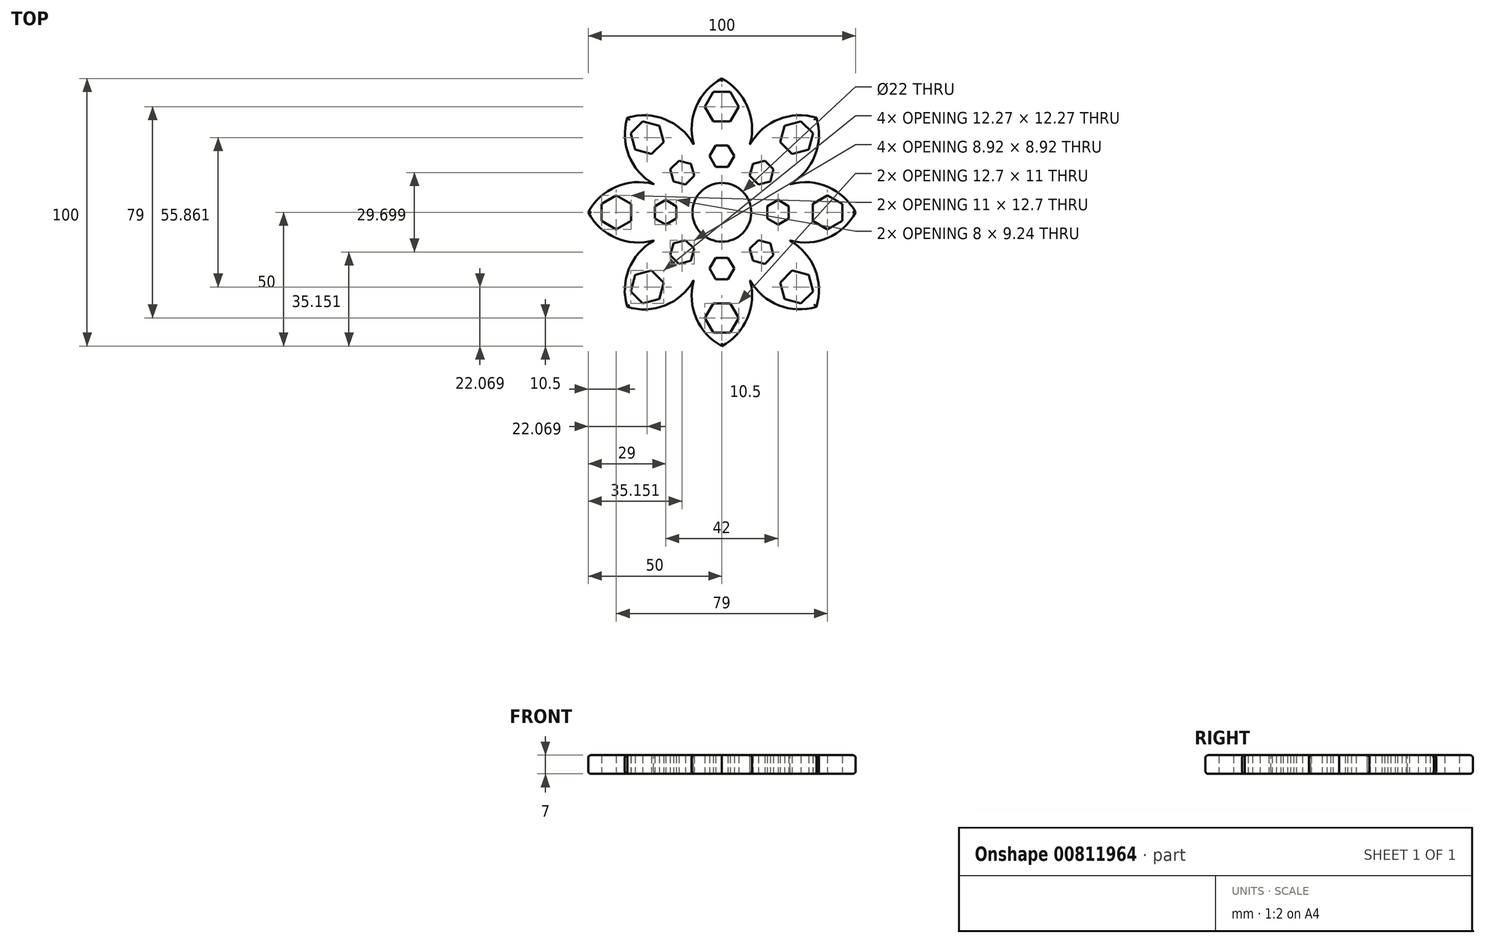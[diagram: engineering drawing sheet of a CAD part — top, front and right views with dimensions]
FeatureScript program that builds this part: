
annotation { "Feature Type Name" : "Feature", "Feature Type Description" : "" }
export const myFeature = defineFeature(function(context is Context, id is Id, definition is map)
    precondition{}
    {
        {
            var Q0;
            Q0=qCreatedBy(makeId("Top.planeOp"),FACE);
            var sketch = newSketch(context, id + "F0", { "sketchPlane" : qUnion([Q0])});
            skCircle(sketch, "E0", {"center": v(0, 0) * mm, "radius": 11 * mm});
            skLineSegment(sketch, "E1", {"start": v(0, 74.6) * mm, "end": v(0, -73.86) * mm, "construction": true});
            skLineSegment(sketch, "E2", {"start": v(-71.42, 0) * mm, "end": v(71.7, 0) * mm, "construction": true});
            skLineSegment(sketch, "E3", {"start": v(75.06, 75.06) * mm, "end": v(0, 0) * mm, "construction": true});
            skLineSegment(sketch, "E4", {"start": v(0, 0) * mm, "end": v(-70.75, -70.75) * mm, "construction": true});
            skLineSegment(sketch, "E5", {"start": v(-75.13, 75.13) * mm, "end": v(0, 0) * mm, "construction": true});
            skCircle(sketch, "E6.cCircle", {"center": v(0, 0) * mm, "radius": 21 * mm, "construction": true});
            skLineSegment(sketch, "E6.0", {"start": v(-8.7, 21) * mm, "end": v(8.7, 21) * mm});
            skLineSegment(sketch, "E6.1", {"start": v(8.7, 21) * mm, "end": v(21, 8.7) * mm});
            skLineSegment(sketch, "E6.2", {"start": v(21, 8.7) * mm, "end": v(21, -8.7) * mm});
            skLineSegment(sketch, "E6.3", {"start": v(21, -8.7) * mm, "end": v(8.7, -21) * mm});
            skLineSegment(sketch, "E6.4", {"start": v(8.7, -21) * mm, "end": v(-8.7, -21) * mm});
            skLineSegment(sketch, "E6.5", {"start": v(-8.7, -21) * mm, "end": v(-21, -8.7) * mm});
            skLineSegment(sketch, "E6.6", {"start": v(-21, -8.7) * mm, "end": v(-21, 8.7) * mm});
            skLineSegment(sketch, "E6.7", {"start": v(-21, 8.7) * mm, "end": v(-8.7, 21) * mm});
            skPoint(sketch, "E6.0.midPoint", {"position": v(0, 21) * mm});
            skLineSegment(sketch, "E7", {"start": v(0, 21) * mm, "end": v(0, 50) * mm});
            skLineSegment(sketch, "E8", {"start": v(14.85, 14.85) * mm, "end": v(35.38, 35.38) * mm});
            skLineSegment(sketch, "E9", {"start": v(21, 0) * mm, "end": v(50, 0) * mm});
            skLineSegment(sketch, "E10", {"start": v(14.85, -14.85) * mm, "end": v(35.36, -35.36) * mm});
            skLineSegment(sketch, "E11", {"start": v(0, -21) * mm, "end": v(0, -50) * mm});
            skLineSegment(sketch, "E12", {"start": v(-14.85, -14.85) * mm, "end": v(-35.38, -35.38) * mm});
            skLineSegment(sketch, "E13", {"start": v(-21, 0) * mm, "end": v(-50, 0) * mm});
            skLineSegment(sketch, "E14", {"start": v(-14.85, 14.85) * mm, "end": v(-35.36, 35.36) * mm});
            skArc(sketch, "E15", {"start": v(0, 50) * mm, "mid": v(-10.4, 37.31) * mm, "end": v(-8.7, 21) * mm});
            skArc(sketch, "E16.MirrorCS", {"start": v(0, 50) * mm, "mid": v(10.4, 37.31) * mm, "end": v(8.7, 21) * mm});
            skArc(sketch, "E17", {"start": v(35.38, 35.38) * mm, "mid": v(19.04, 33.76) * mm, "end": v(8.7, 21) * mm});
            skArc(sketch, "E18.MirrorCS", {"start": v(35.38, 35.38) * mm, "mid": v(33.76, 19.04) * mm, "end": v(21, 8.7) * mm});
            skArc(sketch, "E19", {"start": v(50, 0) * mm, "mid": v(37.31, 10.4) * mm, "end": v(21, 8.7) * mm});
            skArc(sketch, "E20.MirrorCS", {"start": v(50, 0) * mm, "mid": v(37.31, -10.4) * mm, "end": v(21, -8.7) * mm});
            skArc(sketch, "E21", {"start": v(35.36, -35.36) * mm, "mid": v(33.74, -19.03) * mm, "end": v(21, -8.7) * mm});
            skArc(sketch, "E22.MirrorCS", {"start": v(35.36, -35.36) * mm, "mid": v(19.03, -33.74) * mm, "end": v(8.7, -21) * mm});
            skArc(sketch, "E23", {"start": v(0, -50) * mm, "mid": v(10.4, -37.31) * mm, "end": v(8.7, -21) * mm});
            skArc(sketch, "E24.MirrorCS", {"start": v(0, -50) * mm, "mid": v(-10.4, -37.31) * mm, "end": v(-8.7, -21) * mm});
            skArc(sketch, "E25", {"start": v(-35.38, -35.38) * mm, "mid": v(-19.04, -33.76) * mm, "end": v(-8.7, -21) * mm});
            skArc(sketch, "E26.MirrorCS", {"start": v(-35.38, -35.38) * mm, "mid": v(-33.76, -19.04) * mm, "end": v(-21, -8.7) * mm});
            skArc(sketch, "E27", {"start": v(-50, 0) * mm, "mid": v(-37.31, -10.4) * mm, "end": v(-21, -8.7) * mm});
            skArc(sketch, "E28.MirrorCS", {"start": v(-50, 0) * mm, "mid": v(-37.31, 10.4) * mm, "end": v(-21, 8.7) * mm});
            skArc(sketch, "E29", {"start": v(-35.36, 35.36) * mm, "mid": v(-33.74, 19.03) * mm, "end": v(-21, 8.7) * mm});
            skArc(sketch, "E30.MirrorCS", {"start": v(-35.36, 35.36) * mm, "mid": v(-19.03, 33.74) * mm, "end": v(-8.7, 21) * mm});
            skCircle(sketch, "E31.cCircle", {"center": v(27.93, 27.93) * mm, "radius": 5.5 * mm, "construction": true});
            skLineSegment(sketch, "E31.0", {"start": v(23.44, 32.42) * mm, "end": v(29.57, 34.07) * mm});
            skLineSegment(sketch, "E31.1", {"start": v(29.57, 34.07) * mm, "end": v(34.07, 29.57) * mm});
            skLineSegment(sketch, "E31.2", {"start": v(34.07, 29.57) * mm, "end": v(32.42, 23.44) * mm});
            skLineSegment(sketch, "E31.3", {"start": v(32.42, 23.44) * mm, "end": v(26.29, 21.8) * mm});
            skLineSegment(sketch, "E31.4", {"start": v(26.29, 21.8) * mm, "end": v(21.8, 26.29) * mm});
            skLineSegment(sketch, "E31.5", {"start": v(21.8, 26.29) * mm, "end": v(23.44, 32.42) * mm});
            skPoint(sketch, "E31.0.midPoint", {"position": v(26.5, 33.24) * mm});
            skCircle(sketch, "E32.cCircle", {"center": v(39.5, 0) * mm, "radius": 5.5 * mm, "construction": true});
            skLineSegment(sketch, "E32.0", {"start": v(39.5, 6.35) * mm, "end": v(45, 3.18) * mm});
            skLineSegment(sketch, "E32.1", {"start": v(45, 3.18) * mm, "end": v(45, -3.18) * mm});
            skLineSegment(sketch, "E32.2", {"start": v(45, -3.18) * mm, "end": v(39.5, -6.35) * mm});
            skLineSegment(sketch, "E32.3", {"start": v(39.5, -6.35) * mm, "end": v(34, -3.18) * mm});
            skLineSegment(sketch, "E32.4", {"start": v(34, -3.18) * mm, "end": v(34, 3.18) * mm});
            skLineSegment(sketch, "E32.5", {"start": v(34, 3.18) * mm, "end": v(39.5, 6.35) * mm});
            skPoint(sketch, "E32.0.midPoint", {"position": v(42.25, 4.76) * mm});
            skCircle(sketch, "E33.cCircle", {"center": v(-27.93, -27.93) * mm, "radius": 5.5 * mm, "construction": true});
            skLineSegment(sketch, "E33.0", {"start": v(-23.44, -32.42) * mm, "end": v(-29.57, -34.07) * mm});
            skLineSegment(sketch, "E33.1", {"start": v(-29.57, -34.07) * mm, "end": v(-34.07, -29.57) * mm});
            skLineSegment(sketch, "E33.2", {"start": v(-34.07, -29.57) * mm, "end": v(-32.42, -23.44) * mm});
            skLineSegment(sketch, "E33.3", {"start": v(-32.42, -23.44) * mm, "end": v(-26.29, -21.8) * mm});
            skLineSegment(sketch, "E33.4", {"start": v(-26.29, -21.8) * mm, "end": v(-21.8, -26.29) * mm});
            skLineSegment(sketch, "E33.5", {"start": v(-21.8, -26.29) * mm, "end": v(-23.44, -32.42) * mm});
            skPoint(sketch, "E33.0.midPoint", {"position": v(-26.5, -33.24) * mm});
            skCircle(sketch, "E34.cCircle", {"center": v(-39.5, 0) * mm, "radius": 5.5 * mm, "construction": true});
            skLineSegment(sketch, "E34.0", {"start": v(-34, -3.18) * mm, "end": v(-39.5, -6.35) * mm});
            skLineSegment(sketch, "E34.1", {"start": v(-39.5, -6.35) * mm, "end": v(-45, -3.18) * mm});
            skLineSegment(sketch, "E34.2", {"start": v(-45, -3.18) * mm, "end": v(-45, 3.18) * mm});
            skLineSegment(sketch, "E34.3", {"start": v(-45, 3.18) * mm, "end": v(-39.5, 6.35) * mm});
            skLineSegment(sketch, "E34.4", {"start": v(-39.5, 6.35) * mm, "end": v(-34, 3.18) * mm});
            skLineSegment(sketch, "E34.5", {"start": v(-34, 3.18) * mm, "end": v(-34, -3.18) * mm});
            skPoint(sketch, "E34.0.midPoint", {"position": v(-36.75, -4.76) * mm});
            skCircle(sketch, "E35.cCircle", {"center": v(-27.93, 27.93) * mm, "radius": 5.5 * mm, "construction": true});
            skLineSegment(sketch, "E35.0", {"start": v(-29.57, 34.07) * mm, "end": v(-23.44, 32.42) * mm});
            skLineSegment(sketch, "E35.1", {"start": v(-23.44, 32.42) * mm, "end": v(-21.8, 26.29) * mm});
            skLineSegment(sketch, "E35.2", {"start": v(-21.8, 26.29) * mm, "end": v(-26.29, 21.8) * mm});
            skLineSegment(sketch, "E35.3", {"start": v(-26.29, 21.8) * mm, "end": v(-32.42, 23.44) * mm});
            skLineSegment(sketch, "E35.4", {"start": v(-32.42, 23.44) * mm, "end": v(-34.07, 29.57) * mm});
            skLineSegment(sketch, "E35.5", {"start": v(-34.07, 29.57) * mm, "end": v(-29.57, 34.07) * mm});
            skPoint(sketch, "E35.0.midPoint", {"position": v(-26.5, 33.24) * mm});
            skCircle(sketch, "E36.cCircle", {"center": v(27.93, -27.93) * mm, "radius": 5.5 * mm, "construction": true});
            skLineSegment(sketch, "E36.0", {"start": v(26.29, -21.8) * mm, "end": v(32.42, -23.44) * mm});
            skLineSegment(sketch, "E36.1", {"start": v(32.42, -23.44) * mm, "end": v(34.07, -29.57) * mm});
            skLineSegment(sketch, "E36.2", {"start": v(34.07, -29.57) * mm, "end": v(29.57, -34.07) * mm});
            skLineSegment(sketch, "E36.3", {"start": v(29.57, -34.07) * mm, "end": v(23.44, -32.42) * mm});
            skLineSegment(sketch, "E36.4", {"start": v(23.44, -32.42) * mm, "end": v(21.8, -26.29) * mm});
            skLineSegment(sketch, "E36.5", {"start": v(21.8, -26.29) * mm, "end": v(26.29, -21.8) * mm});
            skCircle(sketch, "E37.cCircle", {"center": v(0, 39.5) * mm, "radius": 5.5 * mm, "construction": true});
            skLineSegment(sketch, "E37.0", {"start": v(6.35, 39.5) * mm, "end": v(3.18, 34) * mm});
            skLineSegment(sketch, "E37.1", {"start": v(3.18, 34) * mm, "end": v(-3.18, 34) * mm});
            skLineSegment(sketch, "E37.2", {"start": v(-3.18, 34) * mm, "end": v(-6.35, 39.5) * mm});
            skLineSegment(sketch, "E37.3", {"start": v(-6.35, 39.5) * mm, "end": v(-3.18, 45) * mm});
            skLineSegment(sketch, "E37.4", {"start": v(-3.18, 45) * mm, "end": v(3.18, 45) * mm});
            skLineSegment(sketch, "E37.5", {"start": v(3.18, 45) * mm, "end": v(6.35, 39.5) * mm});
            skPoint(sketch, "E37.0.midPoint", {"position": v(4.76, 36.75) * mm});
            skCircle(sketch, "E38.cCircle", {"center": v(0, -39.5) * mm, "radius": 5.5 * mm, "construction": true});
            skLineSegment(sketch, "E38.0", {"start": v(6.35, -39.5) * mm, "end": v(3.18, -45) * mm});
            skLineSegment(sketch, "E38.1", {"start": v(3.18, -45) * mm, "end": v(-3.18, -45) * mm});
            skLineSegment(sketch, "E38.2", {"start": v(-3.18, -45) * mm, "end": v(-6.35, -39.5) * mm});
            skLineSegment(sketch, "E38.3", {"start": v(-6.35, -39.5) * mm, "end": v(-3.18, -34) * mm});
            skLineSegment(sketch, "E38.4", {"start": v(-3.18, -34) * mm, "end": v(3.18, -34) * mm});
            skLineSegment(sketch, "E38.5", {"start": v(3.18, -34) * mm, "end": v(6.35, -39.5) * mm});
            skPoint(sketch, "E38.0.midPoint", {"position": v(4.76, -42.25) * mm});
            skCircle(sketch, "E39.cCircle", {"center": v(-14.85, 14.85) * mm, "radius": 4 * mm, "construction": true});
            skLineSegment(sketch, "E39.0", {"start": v(-19.31, 16.04) * mm, "end": v(-16.04, 19.31) * mm});
            skLineSegment(sketch, "E39.1", {"start": v(-16.04, 19.31) * mm, "end": v(-11.58, 18.12) * mm});
            skLineSegment(sketch, "E39.2", {"start": v(-11.58, 18.12) * mm, "end": v(-10.39, 13.65) * mm});
            skLineSegment(sketch, "E39.3", {"start": v(-10.39, 13.65) * mm, "end": v(-13.65, 10.39) * mm});
            skLineSegment(sketch, "E39.4", {"start": v(-13.65, 10.39) * mm, "end": v(-18.12, 11.58) * mm});
            skLineSegment(sketch, "E39.5", {"start": v(-18.12, 11.58) * mm, "end": v(-19.31, 16.04) * mm});
            skPoint(sketch, "E39.0.midPoint", {"position": v(-17.68, 17.68) * mm});
            skLineSegment(sketch, "E40.MirrorCS", {"start": v(16.04, -19.31) * mm, "end": v(19.31, -16.04) * mm});
            skLineSegment(sketch, "E41.MirrorCS", {"start": v(18.12, -11.58) * mm, "end": v(13.65, -10.39) * mm});
            skLineSegment(sketch, "E42.MirrorCS", {"start": v(19.31, -16.04) * mm, "end": v(18.12, -11.58) * mm});
            skLineSegment(sketch, "E43.MirrorCS", {"start": v(10.39, -13.65) * mm, "end": v(11.58, -18.12) * mm});
            skLineSegment(sketch, "E44.MirrorCS", {"start": v(13.65, -10.39) * mm, "end": v(10.39, -13.65) * mm});
            skCircle(sketch, "E45.MirrorC", {"center": v(14.85, -14.85) * mm, "radius": 4 * mm, "construction": true});
            skPoint(sketch, "E46.MirrorP", {"position": v(17.68, -17.68) * mm});
            skLineSegment(sketch, "E47.MirrorCS", {"start": v(11.58, -18.12) * mm, "end": v(16.04, -19.31) * mm});
            skLineSegment(sketch, "E48.MirrorCS", {"start": v(19.31, 16.04) * mm, "end": v(16.04, 19.31) * mm});
            skLineSegment(sketch, "E49.MirrorCS", {"start": v(11.58, 18.12) * mm, "end": v(10.39, 13.65) * mm});
            skLineSegment(sketch, "E50.MirrorCS", {"start": v(18.12, 11.58) * mm, "end": v(19.31, 16.04) * mm});
            skLineSegment(sketch, "E51.MirrorCS", {"start": v(13.65, 10.39) * mm, "end": v(18.12, 11.58) * mm});
            skLineSegment(sketch, "E52.MirrorCS", {"start": v(16.04, 19.31) * mm, "end": v(11.58, 18.12) * mm});
            skCircle(sketch, "E53.MirrorC", {"center": v(14.85, 14.85) * mm, "radius": 4 * mm, "construction": true});
            skLineSegment(sketch, "E54.MirrorCS", {"start": v(10.39, 13.65) * mm, "end": v(13.65, 10.39) * mm});
            skLineSegment(sketch, "E55.MirrorCS", {"start": v(-16.04, -19.31) * mm, "end": v(-19.31, -16.04) * mm});
            skLineSegment(sketch, "E56.MirrorCS", {"start": v(-18.12, -11.58) * mm, "end": v(-13.65, -10.39) * mm});
            skLineSegment(sketch, "E57.MirrorCS", {"start": v(-10.39, -13.65) * mm, "end": v(-11.58, -18.12) * mm});
            skCircle(sketch, "E58.MirrorC", {"center": v(-14.85, -14.85) * mm, "radius": 4 * mm, "construction": true});
            skLineSegment(sketch, "E59.MirrorCS", {"start": v(-11.58, -18.12) * mm, "end": v(-16.04, -19.31) * mm});
            skPoint(sketch, "E60.MirrorP", {"position": v(-17.68, -17.68) * mm});
            skLineSegment(sketch, "E61.MirrorCS", {"start": v(-13.65, -10.39) * mm, "end": v(-10.39, -13.65) * mm});
            skLineSegment(sketch, "E62.MirrorCS", {"start": v(-19.31, -16.04) * mm, "end": v(-18.12, -11.58) * mm});
            skCircle(sketch, "E63.cCircle", {"center": v(0, 21) * mm, "radius": 4 * mm, "construction": true});
            skLineSegment(sketch, "E63.0", {"start": v(2.3, 25) * mm, "end": v(4.62, 21) * mm});
            skLineSegment(sketch, "E63.1", {"start": v(4.62, 21) * mm, "end": v(2.3, 17) * mm});
            skLineSegment(sketch, "E63.2", {"start": v(2.3, 17) * mm, "end": v(-2.3, 17) * mm});
            skLineSegment(sketch, "E63.3", {"start": v(-2.3, 17) * mm, "end": v(-4.62, 21) * mm});
            skLineSegment(sketch, "E63.4", {"start": v(-4.62, 21) * mm, "end": v(-2.3, 25) * mm});
            skLineSegment(sketch, "E63.5", {"start": v(-2.3, 25) * mm, "end": v(2.3, 25) * mm});
            skPoint(sketch, "E63.0.midPoint", {"position": v(3.46, 23) * mm});
            skLineSegment(sketch, "E64.MirrorCS", {"start": v(2.3, -25) * mm, "end": v(4.62, -21) * mm});
            skLineSegment(sketch, "E65.MirrorCS", {"start": v(-2.3, -25) * mm, "end": v(2.3, -25) * mm});
            skLineSegment(sketch, "E66.MirrorCS", {"start": v(2.3, -17) * mm, "end": v(-2.3, -17) * mm});
            skPoint(sketch, "E67.MirrorP", {"position": v(0, -21) * mm});
            skLineSegment(sketch, "E68.MirrorCS", {"start": v(-4.62, -21) * mm, "end": v(-2.3, -25) * mm});
            skPoint(sketch, "E69.MirrorP", {"position": v(3.46, -23) * mm});
            skLineSegment(sketch, "E70.MirrorCS", {"start": v(-2.3, -17) * mm, "end": v(-4.62, -21) * mm});
            skCircle(sketch, "E71.MirrorC", {"center": v(0, -21) * mm, "radius": 4 * mm, "construction": true});
            skLineSegment(sketch, "E72.MirrorCS", {"start": v(4.62, -21) * mm, "end": v(2.3, -17) * mm});
            skLineSegment(sketch, "E73.MirrorCS", {"start": v(-21, 4.62) * mm, "end": v(-25, 2.3) * mm});
            skLineSegment(sketch, "E74.MirrorCS", {"start": v(-17, 2.3) * mm, "end": v(-21, 4.62) * mm});
            skLineSegment(sketch, "E75.MirrorCS", {"start": v(-21, -4.62) * mm, "end": v(-17, -2.3) * mm});
            skLineSegment(sketch, "E76.MirrorCS", {"start": v(-25, -2.3) * mm, "end": v(-21, -4.62) * mm});
            skLineSegment(sketch, "E77.MirrorCS", {"start": v(-25, 2.3) * mm, "end": v(-25, -2.3) * mm});
            skPoint(sketch, "E78.MirrorP", {"position": v(-21, 0) * mm});
            skCircle(sketch, "E79.MirrorC", {"center": v(-21, 0) * mm, "radius": 4 * mm, "construction": true});
            skLineSegment(sketch, "E80.MirrorCS", {"start": v(-17, -2.3) * mm, "end": v(-17, 2.3) * mm});
            skPoint(sketch, "E81.MirrorP", {"position": v(-23, -3.46) * mm});
            skLineSegment(sketch, "E82.MirrorCS", {"start": v(21, 4.62) * mm, "end": v(25, 2.3) * mm});
            skLineSegment(sketch, "E83.MirrorCS", {"start": v(21, -4.62) * mm, "end": v(17, -2.3) * mm});
            skLineSegment(sketch, "E84.MirrorCS", {"start": v(17, -2.3) * mm, "end": v(17, 2.3) * mm});
            skLineSegment(sketch, "E85.MirrorCS", {"start": v(25, -2.3) * mm, "end": v(21, -4.62) * mm});
            skLineSegment(sketch, "E86.MirrorCS", {"start": v(25, 2.3) * mm, "end": v(25, -2.3) * mm});
            skPoint(sketch, "E87.MirrorP", {"position": v(21, 0) * mm});
            skPoint(sketch, "E88.MirrorP", {"position": v(23, -3.46) * mm});
            skLineSegment(sketch, "E89.MirrorCS", {"start": v(17, 2.3) * mm, "end": v(21, 4.62) * mm});
            skCircle(sketch, "E90.MirrorC", {"center": v(21, 0) * mm, "radius": 4 * mm, "construction": true});
            skSolve(sketch);
        }
        {
            var Q0;
            Q0 = qSketchRegion(id + "F0", true);
            var Q1;
            Q1=makeQuery(id+"F0.imprint","IMPRINT",FACE,{"disambiguationData":[TD([[makeQuery(id+"F0.imprint","IMPRINT",EDGE,{"derivedFrom":sQuery(id+"F0.wireOp",EDGE,"E0")}),-1.0]])]});
            extrude(context, id + "F1", {"entities" : qUnion([Q0, Q1]), "depth" : 7 * mm, "offsetDistance" : 25 * mm});
        }
        {
            var Q0;
            Q0=makeQuery(id+"F1.opExtrude","SWEPT_EDGE",EDGE,{"disambiguationData":[OSD([sQuery(id+"F0.wireOp",EDGE,"E22.MirrorCS"),sQuery(id+"F0.wireOp",EDGE,"E23")])]});
            var Q1;
            Q1=makeQuery(id+"F1.opExtrude","SWEPT_EDGE",EDGE,{"disambiguationData":[OSD([sQuery(id+"F0.wireOp",EDGE,"E20.MirrorCS"),sQuery(id+"F0.wireOp",EDGE,"E21")])]});
            var Q2;
            Q2=makeQuery(id+"F1.opExtrude","SWEPT_EDGE",EDGE,{"disambiguationData":[OSD([sQuery(id+"F0.wireOp",EDGE,"E18.MirrorCS"),sQuery(id+"F0.wireOp",EDGE,"E19")])]});
            var Q3;
            Q3=makeQuery(id+"F1.opExtrude","SWEPT_EDGE",EDGE,{"disambiguationData":[OSD([sQuery(id+"F0.wireOp",EDGE,"E16.MirrorCS"),sQuery(id+"F0.wireOp",EDGE,"E17")])]});
            var Q4;
            Q4=makeQuery(id+"F1.opExtrude","SWEPT_EDGE",EDGE,{"disambiguationData":[OSD([sQuery(id+"F0.wireOp",EDGE,"E15"),sQuery(id+"F0.wireOp",EDGE,"E30.MirrorCS")])]});
            var Q5;
            Q5=makeQuery(id+"F1.opExtrude","SWEPT_EDGE",EDGE,{"disambiguationData":[OSD([sQuery(id+"F0.wireOp",EDGE,"E28.MirrorCS"),sQuery(id+"F0.wireOp",EDGE,"E29")])]});
            var Q6;
            Q6=makeQuery(id+"F1.opExtrude","SWEPT_EDGE",EDGE,{"disambiguationData":[OSD([sQuery(id+"F0.wireOp",EDGE,"E26.MirrorCS"),sQuery(id+"F0.wireOp",EDGE,"E27")])]});
            var Q7;
            Q7=makeQuery(id+"F1.opExtrude","SWEPT_EDGE",EDGE,{"disambiguationData":[OSD([sQuery(id+"F0.wireOp",EDGE,"E24.MirrorCS"),sQuery(id+"F0.wireOp",EDGE,"E25")])]});
            fillet(context, id + "F2", {"entities" : qUnion([Q0, Q1, Q2, Q3, Q4, Q5, Q6, Q7]), "radius" : 0.05 * mm, "tangentPropagation" : true, "allowEdgeOverflow" : false});
        }
        {
            var Q0;
            Q0=makeQuery(id+"F1.opExtrude","CAP_EDGE",EDGE,{"disambiguationData":[OSD([sQuery(id+"F0.wireOp",EDGE,"E25")])],"isStart":true});
            var Q1;
            Q1=makeQuery(id+"F1.opExtrude","CAP_EDGE",EDGE,{"disambiguationData":[OSD([sQuery(id+"F0.wireOp",EDGE,"E23")])],"isStart":true});
            var Q2;
            Q2=makeQuery(id+"F1.opExtrude","CAP_EDGE",EDGE,{"disambiguationData":[OSD([sQuery(id+"F0.wireOp",EDGE,"E23")])],"isStart":false});
            var Q3;
            Q3=makeQuery(id+"F1.opExtrude","CAP_EDGE",EDGE,{"disambiguationData":[OSD([sQuery(id+"F0.wireOp",EDGE,"E24.MirrorCS")])],"isStart":false});
            var Q4;
            Q4=makeQuery(id+"F1.opExtrude","CAP_EDGE",EDGE,{"disambiguationData":[OSD([sQuery(id+"F0.wireOp",EDGE,"E26.MirrorCS")])],"isStart":true});
            var Q5;
            Q5=makeQuery(id+"F1.opExtrude","CAP_EDGE",EDGE,{"disambiguationData":[OSD([sQuery(id+"F0.wireOp",EDGE,"E26.MirrorCS")])],"isStart":false});
            var Q6;
            Q6=makeQuery(id+"F1.opExtrude","CAP_EDGE",EDGE,{"disambiguationData":[OSD([sQuery(id+"F0.wireOp",EDGE,"E16.MirrorCS")])],"isStart":true});
            var Q7;
            Q7=makeQuery(id+"F1.opExtrude","CAP_EDGE",EDGE,{"disambiguationData":[OSD([sQuery(id+"F0.wireOp",EDGE,"E16.MirrorCS")])],"isStart":false});
            var Q8;
            Q8=makeQuery(id+"F1.opExtrude","CAP_EDGE",EDGE,{"disambiguationData":[OSD([sQuery(id+"F0.wireOp",EDGE,"E15")])],"isStart":true});
            var Q9;
            Q9=makeQuery(id+"F1.opExtrude","CAP_EDGE",EDGE,{"disambiguationData":[OSD([sQuery(id+"F0.wireOp",EDGE,"E15")])],"isStart":false});
            var Q10;
            Q10=makeQuery(id+"F1.opExtrude","CAP_EDGE",EDGE,{"disambiguationData":[OSD([sQuery(id+"F0.wireOp",EDGE,"E29")])],"isStart":false});
            var Q11;
            Q11=makeQuery(id+"F1.opExtrude","CAP_EDGE",EDGE,{"disambiguationData":[OSD([sQuery(id+"F0.wireOp",EDGE,"E29")])],"isStart":true});
            var Q12;
            Q12=makeQuery(id+"F1.opExtrude","CAP_EDGE",EDGE,{"disambiguationData":[OSD([sQuery(id+"F0.wireOp",EDGE,"E21")])],"isStart":true});
            var Q13;
            Q13=makeQuery(id+"F1.opExtrude","CAP_EDGE",EDGE,{"disambiguationData":[OSD([sQuery(id+"F0.wireOp",EDGE,"E21")])],"isStart":false});
            var Q14;
            Q14=makeQuery(id+"F1.opExtrude","CAP_EDGE",EDGE,{"disambiguationData":[OSD([sQuery(id+"F0.wireOp",EDGE,"E19")])],"isStart":true});
            var Q15;
            Q15=makeQuery(id+"F1.opExtrude","CAP_EDGE",EDGE,{"disambiguationData":[OSD([sQuery(id+"F0.wireOp",EDGE,"E18.MirrorCS")])],"isStart":false});
            fillet(context, id + "F3", {"entities" : qUnion([Q0, Q1, Q2, Q3, Q4, Q5, Q6, Q7, Q8, Q9, Q10, Q11, Q12, Q13, Q14, Q15]), "radius" : 1 * mm, "tangentPropagation" : true, "allowEdgeOverflow" : false});
        }
    });
